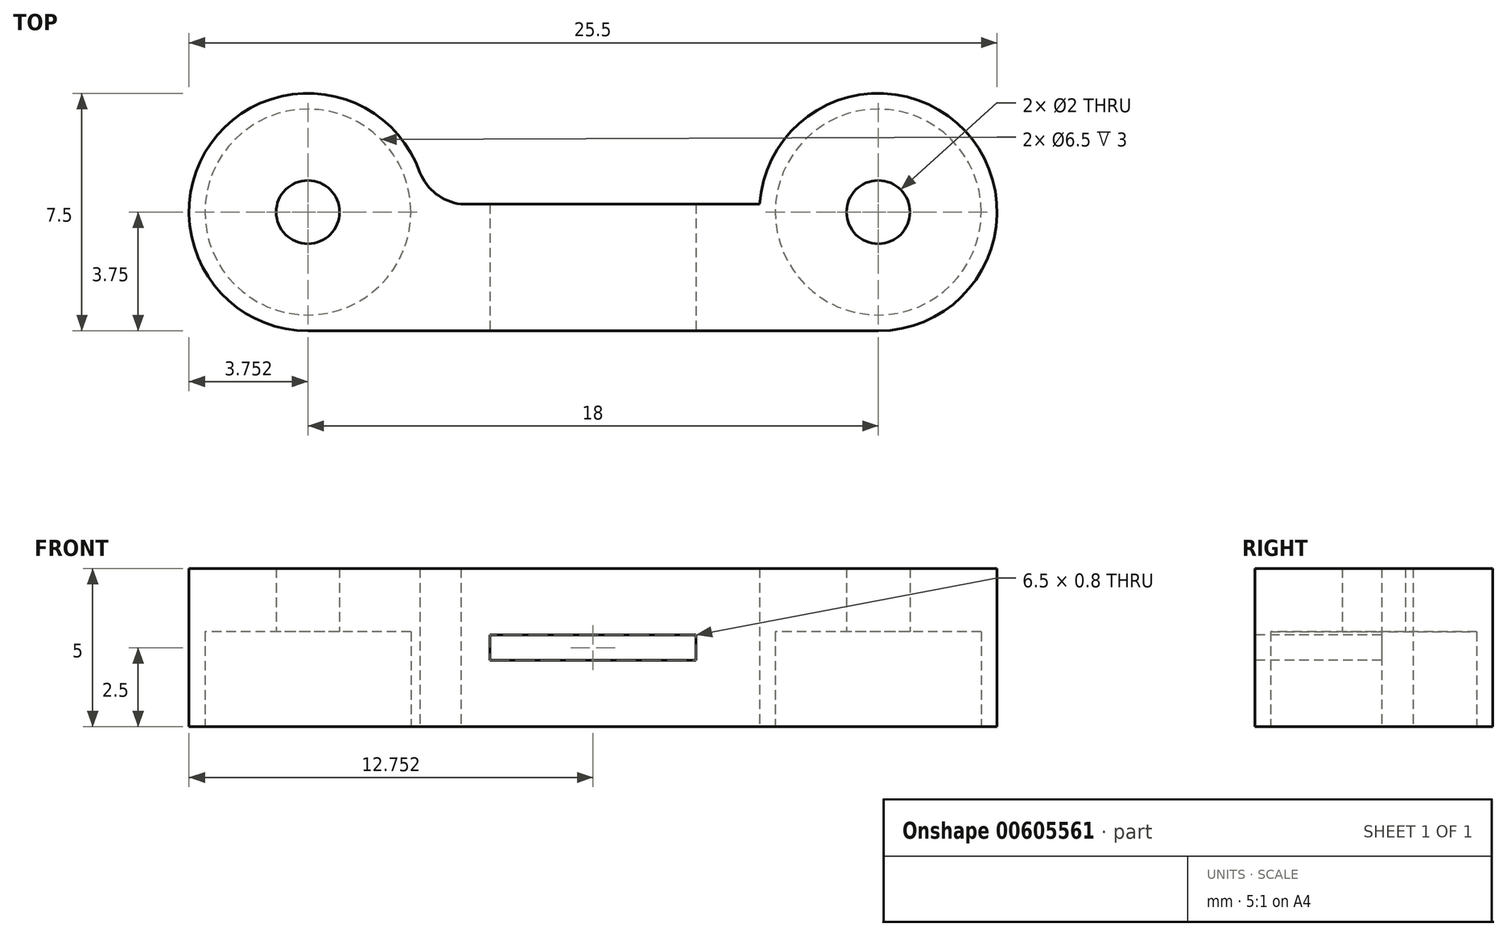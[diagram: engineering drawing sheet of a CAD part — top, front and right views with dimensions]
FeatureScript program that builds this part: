
annotation { "Feature Type Name" : "Feature", "Feature Type Description" : "" }
export const myFeature = defineFeature(function(context is Context, id is Id, definition is map)
    precondition{}
    {
        {
            var Q0;
            Q0=qCreatedBy(makeId("Top.planeOp"),FACE);
            var sketch = newSketch(context, id + "F0", { "sketchPlane" : qUnion([Q0])});
            skLineSegment(sketch, "E0.bottom", {"start": v(-7.92, 1.05) * mm, "end": v(10.08, 1.05) * mm, "construction": true});
            skCircle(sketch, "E1", {"center": v(-7.92, 1.05) * mm, "radius": 3.25 * mm});
            skCircle(sketch, "E2", {"center": v(10.08, 1.05) * mm, "radius": 3.25 * mm});
            skCircle(sketch, "E3", {"center": v(-7.92, 1.05) * mm, "radius": 3.75 * mm});
            skCircle(sketch, "E4", {"center": v(10.08, 1.05) * mm, "radius": 3.75 * mm});
            skLineSegment(sketch, "E5", {"start": v(-7.92, 4.8) * mm, "end": v(10.08, 4.8) * mm, "construction": true});
            skLineSegment(sketch, "E6", {"start": v(10.08, -2.7) * mm, "end": v(-7.92, -2.7) * mm});
            skCircle(sketch, "E7", {"center": v(-7.92, 1.05) * mm, "radius": 1 * mm});
            skCircle(sketch, "E8", {"center": v(10.08, 1.05) * mm, "radius": 1 * mm});
            skLineSegment(sketch, "E9", {"start": v(-7.92, -2.94) * mm, "end": v(-7.92, 5.55) * mm, "construction": true});
            skLineSegment(sketch, "E10", {"start": v(10.08, -2.98) * mm, "end": v(10.08, 5.67) * mm, "construction": true});
            skLineSegment(sketch, "E11", {"start": v(-4.18, 1.3) * mm, "end": v(6.34, 1.3) * mm});
            skArc(sketch, "E12", {"start": v(-4.38, 2.3) * mm, "mid": v(-3.87, 1.62) * mm, "end": v(-3.1, 1.3) * mm});
            skLineSegment(sketch, "E13", {"start": v(1.08, -2.7) * mm, "end": v(1.08, 3.25) * mm, "construction": true});
            skArc(sketch, "E14.MirrorCS", {"start": v(6.55, 2.3) * mm, "mid": v(6.03, 1.62) * mm, "end": v(5.26, 1.3) * mm});
            skSolve(sketch);
        }
        {
            var Q0;
            {var subQ0=sQuery(id+"F0.wireOp",EDGE,"E5");Q0=makeQuery(id+"F0.imprint","IMPRINT",FACE,{"disambiguationData":[TD([[makeQuery(id+"F0.imprint","IMPRINT",EDGE,{"derivedFrom":subQ0}),-1.0]])]});}
            var Q1;
            Q1=makeQuery(id+"F0.imprint","IMPRINT",FACE,{"disambiguationData":[TD([[makeQuery(id+"F0.imprint","IMPRINT",EDGE,{"derivedFrom":sQuery(id+"F0.wireOp",EDGE,"E1")}),-1.0]])]});
            var Q2;
            Q2=makeQuery(id+"F0.imprint","IMPRINT",FACE,{"disambiguationData":[TD([[makeQuery(id+"F0.imprint","IMPRINT",EDGE,{"derivedFrom":sQuery(id+"F0.wireOp",EDGE,"E1")}),1.0]])]});
            var Q3;
            Q3=makeQuery(id+"F0.imprint","IMPRINT",FACE,{"disambiguationData":[TD([[makeQuery(id+"F0.imprint","IMPRINT",EDGE,{"derivedFrom":sQuery(id+"F0.wireOp",EDGE,"E2")}),-1.0]])]});
            var Q4;
            Q4=makeQuery(id+"F0.imprint","IMPRINT",FACE,{"disambiguationData":[TD([[makeQuery(id+"F0.imprint","IMPRINT",EDGE,{"derivedFrom":sQuery(id+"F0.wireOp",EDGE,"E2")}),1.0]])]});
            var Q5;
            {var subQ0=sQuery(id+"F0.wireOp",EDGE,"E6");Q5=makeQuery(id+"F0.imprint","IMPRINT",FACE,{"disambiguationData":[TD([[makeQuery(id+"F0.imprint","IMPRINT",EDGE,{"derivedFrom":subQ0}),-1.0]])]});}
            var Q6;
            {var subQ3=sQuery(id+"F0.wireOp",EDGE,"E12");Q6=makeQuery(id+"F0.imprint","IMPRINT",FACE,{"disambiguationData":[TD([[makeQuery(id+"F0.imprint","IMPRINT",EDGE,{"derivedFrom":subQ3}),-1.0]])]});}
            var Q7;
            {var subQ3=sQuery(id+"F0.wireOp",EDGE,"E14.MirrorCS");Q7=makeQuery(id+"F0.imprint","IMPRINT",FACE,{"disambiguationData":[TD([[makeQuery(id+"F0.imprint","IMPRINT",EDGE,{"derivedFrom":subQ3}),1.0]])]});}
            extrude(context, id + "F1", {"entities" : qUnion([Q0, Q1, Q2, Q3, Q4, Q5, Q6, Q7]), "depth" : 5 * mm, "offsetDistance" : 25 * mm});
        }
        {
            var Q0;
            Q0=makeQuery(id+"F0.imprint","IMPRINT",FACE,{"disambiguationData":[TD([[makeQuery(id+"F0.imprint","IMPRINT",EDGE,{"derivedFrom":sQuery(id+"F0.wireOp",EDGE,"E2")}),1.0]])]});
            var Q1;
            Q1=makeQuery(id+"F0.imprint","IMPRINT",FACE,{"disambiguationData":[TD([[makeQuery(id+"F0.imprint","IMPRINT",EDGE,{"derivedFrom":sQuery(id+"F0.wireOp",EDGE,"E1")}),1.0]])]});
            extrude(context, id + "F2", {"entities" : qUnion([Q0, Q1]), "operationType" : NewBodyOperationType.REMOVE, "depth" : 3 * mm, "offsetDistance" : 25 * mm});
        }
        {
            var Q0;
            Q0=makeQuery(id+"F1.opExtrude","SWEPT_FACE",FACE,{"disambiguationData":[OSD([sQuery(id+"F0.wireOp",EDGE,"E6")])]});
            var sketch = newSketch(context, id + "F3", { "sketchPlane" : qUnion([Q0])});
            skLineSegment(sketch, "E15", {"start": v(1.08, 5) * mm, "end": v(1.08, 0) * mm, "construction": true});
            skLineSegment(sketch, "E16", {"start": v(-7.92, 2.5) * mm, "end": v(10.08, 2.5) * mm, "construction": true});
            skLineSegment(sketch, "E17.bottom", {"start": v(-2.17, 2.1) * mm, "end": v(4.33, 2.1) * mm});
            skLineSegment(sketch, "E17.top", {"start": v(-2.17, 2.9) * mm, "end": v(4.33, 2.9) * mm});
            skLineSegment(sketch, "E17.left", {"start": v(-2.17, 2.1) * mm, "end": v(-2.17, 2.9) * mm});
            skLineSegment(sketch, "E17.right", {"start": v(4.33, 2.1) * mm, "end": v(4.33, 2.9) * mm});
            skPoint(sketch, "E17.middle", {"position": v(1.08, 2.5) * mm});
            skSolve(sketch);
        }
        {
            var Q0;
            Q0=makeQuery(id+"F3.imprint","IMPRINT",FACE,{"disambiguationData":[TD([[makeQuery(id+"F3.imprint","IMPRINT",EDGE,{"derivedFrom":sQuery(id+"F3.wireOp",EDGE,"E17.bottom")}),1.0]])]});
            extrude(context, id + "F4", {"entities" : qUnion([Q0]), "operationType" : NewBodyOperationType.REMOVE, "oppositeDirection" : true, "depth" : 25 * mm, "offsetDistance" : 25 * mm});
        }
    });
